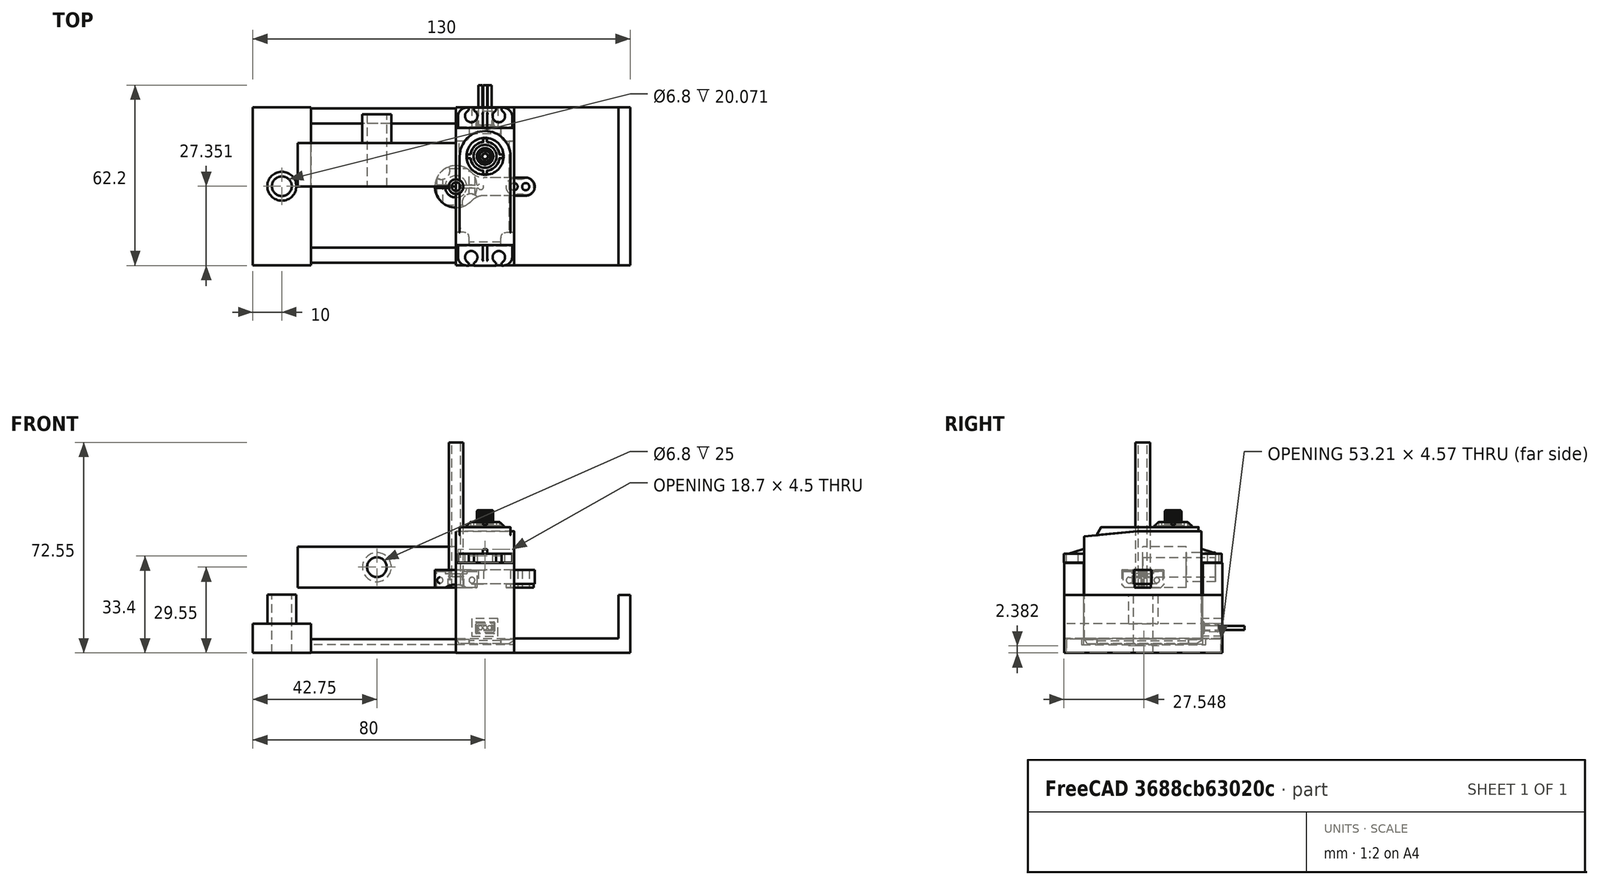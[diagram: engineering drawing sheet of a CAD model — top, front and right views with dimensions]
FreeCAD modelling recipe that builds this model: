
FCSTD DOCUMENT  (FreeCAD 0.19R24366 (Git))
Label: ServoSunFinderSF3218MG
License: All rights reserved
LicenseURL: http://en.wikipedia.org/wiki/All_rights_reserved
objects: Sketcher::SketchObject×15, PartDesign::Pad×10, PartDesign::Pocket×5, App::Part×5, PartDesign::Body×4, Part::Feature×2, Mesh::Feature×1
note: 51 computed .brp shape members not serialized (recipe doc carries the construction recipe); baked Part::Feature solids carry a one-line shape summary decoded from their .brp

FEATURE [Part::Feature] Solid  label="Servo_SF3218MG"
  Placement = pos=(0,0,0) rot=(1,0,0;1.5708rad)
  shape: bbox 20 x 62.45 x 46.03 mm, 436 faces (baked)
FEATURE [Sketcher::SketchObject] Sketch  label="ServoHolder"
  FullyConstrained = false
  MapMode = 4
  Placement = pos=(0,0,0) rot=(0.57735,0.57735,0.57735;2.0944rad)
  sketch-geometry (8):
    g0: LineSegment StartX=-27.0989 StartY=-22.5482 StartZ=0 EndX=27.4011 EndY=-22.5482 EndZ=0
    g1: LineSegment StartX=20.6511 StartY=-19.5482 StartZ=0 EndX=20.6511 EndY=8.45178 EndZ=0
    g2: LineSegment StartX=20.6511 StartY=8.45178 StartZ=0 EndX=27.4011 EndY=8.45178 EndZ=0
    g3: LineSegment StartX=-20.3489 StartY=-19.5482 StartZ=0 EndX=-20.3489 EndY=8.45178 EndZ=0
    g4: LineSegment StartX=-20.3489 StartY=8.45178 StartZ=0 EndX=-27.0989 EndY=8.45178 EndZ=0
    g5: LineSegment StartX=20.6511 StartY=-19.5482 StartZ=0 EndX=-20.3489 EndY=-19.5482 EndZ=0
    g6: LineSegment StartX=-27.0989 StartY=8.45178 StartZ=0 EndX=-27.0989 EndY=-22.5482 EndZ=0
    g7: LineSegment StartX=27.4011 StartY=8.45178 StartZ=0 EndX=27.4011 EndY=-22.5482 EndZ=0
  constraints (22):
    c: Horizontal(g0)
    c: Coincident(g1,g2)
    c: Horizontal(g2)
    c: Vertical(g1)
    c: Coincident(g3,g4)
    c: Horizontal(g4)
    c: Vertical(g3)
    c: Coincident(g5,g1)
    c: Coincident(g5,g3)
    c: Horizontal(g5)
    c: Coincident(g6,g4)
    c: Coincident(g6,g0)
    c: Vertical(g6)
    c: Coincident(g7,g2)
    c: Coincident(g7,g0)
    c: Vertical(g7)
    c: DistanceX(g0,g0) = 54.5
    c: DistanceX(g5,g5) = 41
    c: Equal(g4,g2)
    c: Horizontal(g3,g1)
    c: DistanceY(g0,g1) = 3
    c: DistanceY(g1,g1) = 28
FEATURE [Sketcher::SketchObject] Sketch001  label="WireHoleSketch"
  FullyConstrained = false
  Placement = pos=(0,27.4011,0) rot=(0,0.707107,0.707107;3.14159rad)
  sketch-geometry (4):
    g0: LineSegment StartX=-5.36505 StartY=-10.7623 StartZ=0 EndX=-14.3651 EndY=-10.7623 EndZ=0
    g1: LineSegment StartX=-14.3651 StartY=-10.7623 StartZ=0 EndX=-14.3651 EndY=-16.7623 EndZ=0
    g2: LineSegment StartX=-14.3651 StartY=-16.7623 StartZ=0 EndX=-5.36505 EndY=-16.7623 EndZ=0
    g3: LineSegment StartX=-5.36505 StartY=-16.7623 StartZ=0 EndX=-5.36505 EndY=-10.7623 EndZ=0
  constraints (10):
    c: Coincident(g1,g2)
    c: Coincident(g2,g3)
    c: Coincident(g3,g0)
    c: Horizontal(g0)
    c: Horizontal(g2)
    c: Vertical(g1)
    c: Vertical(g3)
    c: Coincident(g1,g0)
    c: DistanceX(g0,g0) = 9
    c: DistanceY(g1,g1) = 6
FEATURE [PartDesign::Pad] Pad  label="ExtrudeServoHolder"
  Direction = (1,1,1)
  Length = 20
  Length2 = 100
  Placement = pos=(0,0,0) rot=(0.57735,0.57735,0.57735;2.0944rad)
  Profile = -> Sketch
  Type = 0
FEATURE [PartDesign::Pocket] Pocket
  BaseFeature = -> Pad
  Length = 8
  Length2 = 100
  Placement = pos=(0,0,0) rot=(0.57735,0.57735,0.57735;2.0944rad)
  Profile = -> Sketch001
  Type = 0
FEATURE [PartDesign::Body] Body
  Group = -> [Sketch001,Sketch,Pad,Pocket]
  Origin = -> Origin001
  Tip = -> Pocket
FEATURE [App::Part] Part  label="Servo_SF3218MG001"
  Group = -> [Solid,Body]
  Origin = -> Origin
FEATURE [Sketcher::SketchObject] Sketch002  label="ServoHolder002"
  FullyConstrained = false
  MapMode = 4
  Placement = pos=(0,0,0) rot=(0.57735,0.57735,0.57735;2.0944rad)
  sketch-geometry (8):
    g0: LineSegment StartX=-27.0989 StartY=-22.5482 StartZ=0 EndX=27.4011 EndY=-22.5482 EndZ=0
    g1: LineSegment StartX=20.6511 StartY=-19.5482 StartZ=0 EndX=20.6511 EndY=8.45178 EndZ=0
    g2: LineSegment StartX=20.6511 StartY=8.45178 StartZ=0 EndX=27.4011 EndY=8.45178 EndZ=0
    g3: LineSegment StartX=-20.3489 StartY=-19.5482 StartZ=0 EndX=-20.3489 EndY=8.45178 EndZ=0
    g4: LineSegment StartX=-20.3489 StartY=8.45178 StartZ=0 EndX=-27.0989 EndY=8.45178 EndZ=0
    g5: LineSegment StartX=20.6511 StartY=-19.5482 StartZ=0 EndX=-20.3489 EndY=-19.5482 EndZ=0
    g6: LineSegment StartX=-27.0989 StartY=8.45178 StartZ=0 EndX=-27.0989 EndY=-22.5482 EndZ=0
    g7: LineSegment StartX=27.4011 StartY=8.45178 StartZ=0 EndX=27.4011 EndY=-22.5482 EndZ=0
  constraints (22):
    c: Horizontal(g0)
    c: Coincident(g1,g2)
    c: Horizontal(g2)
    c: Vertical(g1)
    c: Coincident(g3,g4)
    c: Horizontal(g4)
    c: Vertical(g3)
    c: Coincident(g5,g1)
    c: Coincident(g5,g3)
    c: Horizontal(g5)
    c: Coincident(g6,g4)
    c: Coincident(g6,g0)
    c: Vertical(g6)
    c: Coincident(g7,g2)
    c: Coincident(g7,g0)
    c: Vertical(g7)
    c: DistanceX(g0,g0) = 54.5
    c: DistanceX(g5,g5) = 41
    c: Equal(g4,g2)
    c: Horizontal(g3,g1)
    c: DistanceY(g0,g1) = 3
    c: DistanceY(g1,g1) = 28
FEATURE [PartDesign::Pad] Pad001  label="ExtrudeServoHolder001"
  Direction = (1,1,1)
  Length = 20
  Length2 = 100
  Placement = pos=(0,0,0) rot=(0.57735,0.57735,0.57735;2.0944rad)
  Profile = -> Sketch002
  Type = 0
FEATURE [Sketcher::SketchObject] Sketch004  label="WireHoleSketch001"
  FullyConstrained = false
  Placement = pos=(0,27.4011,0) rot=(0,0.707107,0.707107;3.14159rad)
  sketch-geometry (4):
    g0: LineSegment StartX=-5.36505 StartY=-10.7623 StartZ=0 EndX=-14.3651 EndY=-10.7623 EndZ=0
    g1: LineSegment StartX=-14.3651 StartY=-10.7623 StartZ=0 EndX=-14.3651 EndY=-16.7623 EndZ=0
    g2: LineSegment StartX=-14.3651 StartY=-16.7623 StartZ=0 EndX=-5.36505 EndY=-16.7623 EndZ=0
    g3: LineSegment StartX=-5.36505 StartY=-16.7623 StartZ=0 EndX=-5.36505 EndY=-10.7623 EndZ=0
  constraints (10):
    c: Coincident(g1,g2)
    c: Coincident(g2,g3)
    c: Coincident(g3,g0)
    c: Horizontal(g0)
    c: Horizontal(g2)
    c: Vertical(g1)
    c: Vertical(g3)
    c: Coincident(g1,g0)
    c: DistanceX(g0,g0) = 9
    c: DistanceY(g1,g1) = 6
FEATURE [PartDesign::Pocket] Pocket001  label="ServoHolder001"
  BaseFeature = -> Pad001
  Length = 8
  Length2 = 100
  Placement = pos=(0,0,0) rot=(0.57735,0.57735,0.57735;2.0944rad)
  Profile = -> Sketch004
  Type = 0
FEATURE [Sketcher::SketchObject] Sketch003  label="HorizontalSupportHole"
  FullyConstrained = false
  MapMode = 5
  Placement = pos=(0,0,0) rot=(0.57735,0.57735,-0.57735;4.18879rad)
  Support = -> [Pocket001]
  sketch-geometry (8):
    g0: LineSegment StartX=-21.0477 StartY=17.881 StartZ=0 EndX=-26.2545 EndY=17.881 EndZ=0
    g1: LineSegment StartX=-26.2545 StartY=17.881 StartZ=0 EndX=-26.2545 EndY=22.4547 EndZ=0
    g2: LineSegment StartX=26.9512 StartY=17.881 StartZ=0 EndX=21.7444 EndY=17.881 EndZ=0
    g3: LineSegment StartX=26.9512 StartY=22.4547 StartZ=0 EndX=26.9512 EndY=17.881 EndZ=0
    g4: LineSegment StartX=21.7444 StartY=19.7543 StartZ=0 EndX=21.7444 EndY=17.881 EndZ=0
    g5: LineSegment StartX=-21.0477 StartY=17.881 StartZ=0 EndX=-21.0477 EndY=19.7543 EndZ=0
    g6: LineSegment StartX=-21.0477 StartY=19.7543 StartZ=0 EndX=21.7444 EndY=19.7543 EndZ=0
    g7: LineSegment StartX=-26.2545 StartY=22.4547 StartZ=0 EndX=26.9512 EndY=22.4547 EndZ=0
  constraints (18):
    c: Coincident(g0,g1)
    c: Horizontal(g0)
    c: Vertical(g1)
    c: Coincident(g3,g2)
    c: Horizontal(g2)
    c: Vertical(g3)
    c: Coincident(g4,g2)
    c: Coincident(g6,g5)
    c: Coincident(g6,g4)
    c: Horizontal(g6)
    c: Coincident(g1,g7)
    c: Horizontal(g7)
    c: Coincident(g3,g7)
    c: Equal(g3,g1)
    c: Equal(g0,g2)
    c: Coincident(g0,g5)
    c: Vertical(g5)
    c: Vertical(g4)
FEATURE [Part::Feature] Solid001  label="ServoHorn"
  shape: bbox 34.33 x 14.81 x 6 mm, 52 faces (baked)
FEATURE [App::Part] Part002  label="ServoHorn001"
  Group = -> [Solid001]
  Origin = -> Origin004
FEATURE [Sketcher::SketchObject] Sketch007
  FullyConstrained = true
  MapMode = 5
  Support = -> [XY_Plane006]
  sketch-geometry (1):
    g0: Circle CenterX=0 CenterY=0 CenterZ=0 NormalX=0 NormalY=0 NormalZ=1 AngleXU=0 Radius=2.5
  constraints (2):
    c: Coincident(g0,g-1)
    c: Diameter(g0) = 5
FEATURE [PartDesign::Pad] Pad002
  Direction = (1,1,1)
  Length = 50
  Length2 = 100
  Profile = -> Sketch007
  Type = 0
FEATURE [Sketcher::SketchObject] Sketch008
  FullyConstrained = true
  MapMode = 5
  Placement = pos=(0,0,50) rot=(0,0,1;0rad)
  Support = -> [Pad002]
  sketch-geometry (1):
    g0: Circle CenterX=0 CenterY=0 CenterZ=0 NormalX=0 NormalY=0 NormalZ=1 AngleXU=0 Radius=1.5
  constraints (2):
    c: Coincident(g0,g-1)
    c: Diameter(g0) = 3
FEATURE [PartDesign::Pocket] Pocket003
  BaseFeature = -> Pad002
  Length = 75
  Length2 = 100
  Profile = -> Sketch008
  Type = 0
FEATURE [PartDesign::Body] Body002
  Group = -> [Sketch007,Pad002,Sketch008,Pocket003]
  Origin = -> Origin006
  Tip = -> Pocket003
FEATURE [App::Part] Part003  label="PostHoleJacket"
  Group = -> [Body002]
  Origin = -> Origin005
FEATURE [Sketcher::SketchObject] Sketch009
  FullyConstrained = true
  MapMode = 5
  Support = -> [XY_Plane008]
  sketch-geometry (4):
    g0: LineSegment StartX=0 StartY=0 StartZ=0 EndX=-54.5 EndY=0 EndZ=0
    g1: LineSegment StartX=-54.5 StartY=0 StartZ=0 EndX=-54.5 EndY=15 EndZ=0
    g2: LineSegment StartX=-54.5 StartY=15 StartZ=0 EndX=0 EndY=15 EndZ=0
    g3: LineSegment StartX=0 StartY=15 StartZ=0 EndX=0 EndY=0 EndZ=0
  constraints (11):
    c: Coincident(g0,g1)
    c: Coincident(g1,g2)
    c: Coincident(g2,g3)
    c: Coincident(g3,g0)
    c: Horizontal(g0)
    c: Horizontal(g2)
    c: Vertical(g1)
    c: Vertical(g3)
    c: Coincident(g0,g-1)
    c: DistanceX(g0,g0) = 54.5
    c: DistanceY(g1,g1) = 15
FEATURE [PartDesign::Pad] Pad003
  Direction = (1,1,1)
  Length = 14
  Length2 = 100
  Profile = -> Sketch009
  Type = 0
FEATURE [Sketcher::SketchObject] Sketch011
  ExternalGeometry = -> [Pad003]
  FullyConstrained = true
  MapMode = 5
  Placement = pos=(0,15,0) rot=(0,0.707107,0.707107;3.14159rad)
  Support = -> [Pad003]
  sketch-geometry (3):
    g0: Circle CenterX=27.25 CenterY=7 CenterZ=0 NormalX=0 NormalY=0 NormalZ=1 AngleXU=0 Radius=5
    g1: LineSegment StartX=27.25 StartY=7 StartZ=0 EndX=0 EndY=7 EndZ=0
    g2: LineSegment StartX=27.25 StartY=7 StartZ=0 EndX=54.5 EndY=7 EndZ=0
  constraints (9):
    c: Diameter(g0) = 10
    c: Coincident(g1,g0)
    c: PointOnObject(g1,g-5)
    c: Horizontal(g1)
    c: Coincident(g2,g0)
    c: PointOnObject(g2,g-4)
    c: Horizontal(g2)
    c: Equal(g1,g2)
    c: DistanceY(g0,g-4) = 7
FEATURE [PartDesign::Pad] Pad005
  BaseFeature = -> Pad003
  Direction = (1,1,1)
  Length = 10
  Length2 = 100
  Profile = -> Sketch011
  Type = 0
FEATURE [Mesh::Feature] Mesh  label="ServoHolderPart (Meshed)"
FEATURE [Sketcher::SketchObject] Sketch012
  ExternalGeometry = -> [Pad005]
  FullyConstrained = true
  MapMode = 5
  Placement = pos=(3e-15,25,-5.1e-15) rot=(0,0.707107,0.707107;3.14159rad)
  Support = -> [Pad005]
  sketch-geometry (1):
    g0: Circle CenterX=27.25 CenterY=7 CenterZ=0 NormalX=0 NormalY=0 NormalZ=1 AngleXU=0 Radius=3.4
  constraints (2):
    c: Coincident(g0,g-3)
    c: Diameter(g0) = 6.8
FEATURE [PartDesign::Pocket] Pocket004
  BaseFeature = -> Pad005
  Length = 30
  Length2 = 100
  Profile = -> Sketch012
  Type = 0
FEATURE [PartDesign::Body] Body003
  Group = -> [Sketch009,Pad003,Sketch011,Pad005,Sketch012,Pocket004]
  Origin = -> Origin008
  Tip = -> Pocket004
FEATURE [App::Part] Part004  label="ServoRudderHolderConnect"
  Group = -> [Body003]
  Origin = -> Origin007
FEATURE [PartDesign::Pad] Pad006
  BaseFeature = -> Pocket001
  Direction = (1,1,1)
  Length = 50
  Length2 = 100
  Placement = pos=(0,0,0) rot=(0.57735,0.57735,0.57735;2.0944rad)
  Profile = -> Sketch003
  Type = 0
FEATURE [Sketcher::SketchObject] Sketch013
  ExternalGeometry = -> [Pad006]
  FullyConstrained = false
  MapMode = 5
  Placement = pos=(-50,1.11e-14,0) rot=(-0.57735,-0.57735,0.57735;2.0944rad)
  Support = -> [Pad006]
  sketch-geometry (4):
    g0: LineSegment StartX=-27.0989 StartY=22.5482 StartZ=0 EndX=27.4011 EndY=22.5482 EndZ=0
    g1: LineSegment StartX=27.4011 StartY=22.5482 StartZ=0 EndX=27.4011 EndY=12.4768 EndZ=0
    g2: LineSegment StartX=27.4011 StartY=12.4768 StartZ=0 EndX=-27.0989 EndY=12.4768 EndZ=0
    g3: LineSegment StartX=-27.0989 StartY=12.4768 StartZ=0 EndX=-27.0989 EndY=22.5482 EndZ=0
  constraints (9):
    c: Coincident(g0,g1)
    c: Coincident(g1,g2)
    c: Coincident(g2,g3)
    c: Coincident(g3,g0)
    c: Horizontal(g2)
    c: Vertical(g1)
    c: Vertical(g3)
    c: Coincident(g0,g-4)
    c: Coincident(g-3,g0)
FEATURE [PartDesign::Pad] Pad007
  BaseFeature = -> Pad006
  Direction = (1,1,1)
  Length = 20
  Length2 = 100
  Placement = pos=(0,0,0) rot=(0.57735,0.57735,0.57735;2.0944rad)
  Profile = -> Sketch013
  Type = 0
FEATURE [Sketcher::SketchObject] Sketch014
  ExternalGeometry = -> [Pad007]
  FullyConstrained = true
  MapMode = 5
  Placement = pos=(1.4e-15,-4.2e-15,-12.4768) rot=(0,0,-1;1.5708rad)
  Support = -> [Pad007]
  sketch-geometry (5):
    g0: Circle CenterX=-0.151063 CenterY=-60 CenterZ=0 NormalX=0 NormalY=0 NormalZ=1 AngleXU=0 Radius=5
    g1: LineSegment StartX=-27.4011 StartY=-60 StartZ=0 EndX=-0.151063 EndY=-60 EndZ=0
    g2: LineSegment StartX=-0.151063 StartY=-60 StartZ=0 EndX=27.0989 EndY=-60 EndZ=0
    g3: LineSegment StartX=-0.151063 StartY=-50 StartZ=0 EndX=-0.151063 EndY=-60 EndZ=0
    g4: LineSegment StartX=-0.151063 StartY=-60 StartZ=0 EndX=-0.151063 EndY=-70 EndZ=0
  constraints (15):
    c: PointOnObject(g1,g-4)
    c: Horizontal(g1)
    c: Coincident(g2,g1)
    c: PointOnObject(g2,g-3)
    c: Horizontal(g2)
    c: Coincident(g0,g1)
    c: Equal(g2,g1)
    c: PointOnObject(g3,g-5)
    c: Coincident(g3,g0)
    c: PointOnObject(g4,g-6)
    c: Vertical(g4)
    c: Equal(g4,g3)
    c: Coincident(g4,g0)
    c: Vertical(g3)
    c: Radius(g0) = 5
FEATURE [PartDesign::Pad] Pad008
  BaseFeature = -> Pad007
  Direction = (1,1,1)
  Length = 10
  Length2 = 100
  Placement = pos=(0,0,0) rot=(0.57735,0.57735,0.57735;2.0944rad)
  Profile = -> Sketch014
  Type = 0
FEATURE [Sketcher::SketchObject] Sketch015
  ExternalGeometry = -> [Pad008]
  FullyConstrained = true
  MapMode = 5
  Placement = pos=(1.1e-15,-9e-16,-2.47682) rot=(0,0,-1;1.5708rad)
  Support = -> [Pad008]
  sketch-geometry (1):
    g0: Circle CenterX=-0.151063 CenterY=-60 CenterZ=0 NormalX=0 NormalY=0 NormalZ=1 AngleXU=0 Radius=3.4
  constraints (2):
    c: Coincident(g0,g-3)
    c: Diameter(g0) = 6.8
FEATURE [PartDesign::Pocket] Pocket005
  BaseFeature = -> Pad008
  Length = 25
  Length2 = 100
  Placement = pos=(0,0,0) rot=(0.57735,0.57735,0.57735;2.0944rad)
  Profile = -> Sketch015
  Type = 0
FEATURE [Sketcher::SketchObject] Sketch016
  ExternalGeometry = -> [Pocket005]
  FullyConstrained = true
  MapMode = 5
  Placement = pos=(20,-1.78e-14,0) rot=(0.57735,0.57735,0.57735;2.0944rad)
  Support = -> [Pocket005]
  sketch-geometry (4):
    g0: LineSegment StartX=-27.0989 StartY=-22.5482 StartZ=0 EndX=27.4011 EndY=-22.5482 EndZ=0
    g1: LineSegment StartX=27.4011 StartY=-22.5482 StartZ=0 EndX=27.4011 EndY=-17.5482 EndZ=0
    g2: LineSegment StartX=27.4011 StartY=-17.5482 StartZ=0 EndX=-27.0989 EndY=-17.5482 EndZ=0
    g3: LineSegment StartX=-27.0989 StartY=-17.5482 StartZ=0 EndX=-27.0989 EndY=-22.5482 EndZ=0
  constraints (11):
    c: Coincident(g0,g1)
    c: Coincident(g1,g2)
    c: Coincident(g2,g3)
    c: Coincident(g3,g0)
    c: Horizontal(g0)
    c: Horizontal(g2)
    c: Vertical(g1)
    c: Vertical(g3)
    c: Coincident(g0,g-5)
    c: PointOnObject(g1,g-4)
    c: DistanceY(g3,g3) = 5
FEATURE [PartDesign::Pad] Pad009
  BaseFeature = -> Pocket005
  Direction = (1,1,1)
  Length = 40
  Length2 = 100
  Placement = pos=(0,0,0) rot=(0.57735,0.57735,0.57735;2.0944rad)
  Profile = -> Sketch016
  Type = 0
FEATURE [Sketcher::SketchObject] Sketch017
  ExternalGeometry = -> [Pad009]
  FullyConstrained = true
  MapMode = 5
  Placement = pos=(0,-3.9e-15,-17.5482) rot=(0,0,-1;1.5708rad)
  Support = -> [Pad009]
  sketch-geometry (4):
    g0: LineSegment StartX=-27.4011 StartY=60 StartZ=0 EndX=27.0989 EndY=60 EndZ=0
    g1: LineSegment StartX=27.0989 StartY=60 StartZ=0 EndX=27.0989 EndY=56 EndZ=0
    g2: LineSegment StartX=27.0989 StartY=56 StartZ=0 EndX=-27.4011 EndY=56 EndZ=0
    g3: LineSegment StartX=-27.4011 StartY=56 StartZ=0 EndX=-27.4011 EndY=60 EndZ=0
  constraints (11):
    c: Coincident(g0,g1)
    c: Coincident(g1,g2)
    c: Coincident(g2,g3)
    c: Coincident(g3,g0)
    c: Horizontal(g0)
    c: Horizontal(g2)
    c: Vertical(g1)
    c: Vertical(g3)
    c: Coincident(g0,g-4)
    c: PointOnObject(g1,g-3)
    c: DistanceY(g1,g1) = 4
FEATURE [PartDesign::Pad] Pad010
  BaseFeature = -> Pad009
  Direction = (1,1,1)
  Length = 15
  Length2 = 100
  Placement = pos=(0,0,0) rot=(0.57735,0.57735,0.57735;2.0944rad)
  Profile = -> Sketch017
  Type = 0
FEATURE [PartDesign::Body] Body001
  Group = -> [Sketch004,Sketch002,Pad001,Pocket001,Sketch003,Pad006,Sketch013,Pad007,Sketch014,Pad008,Sketch015,Pocket005,Sketch016,Pad009,Sketch017,Pad010]
  Origin = -> Origin002
  Tip = -> Pad010
FEATURE [App::Part] Part001  label="ServoHolderPart"
  Group = -> [Body001]
  Origin = -> Origin003
